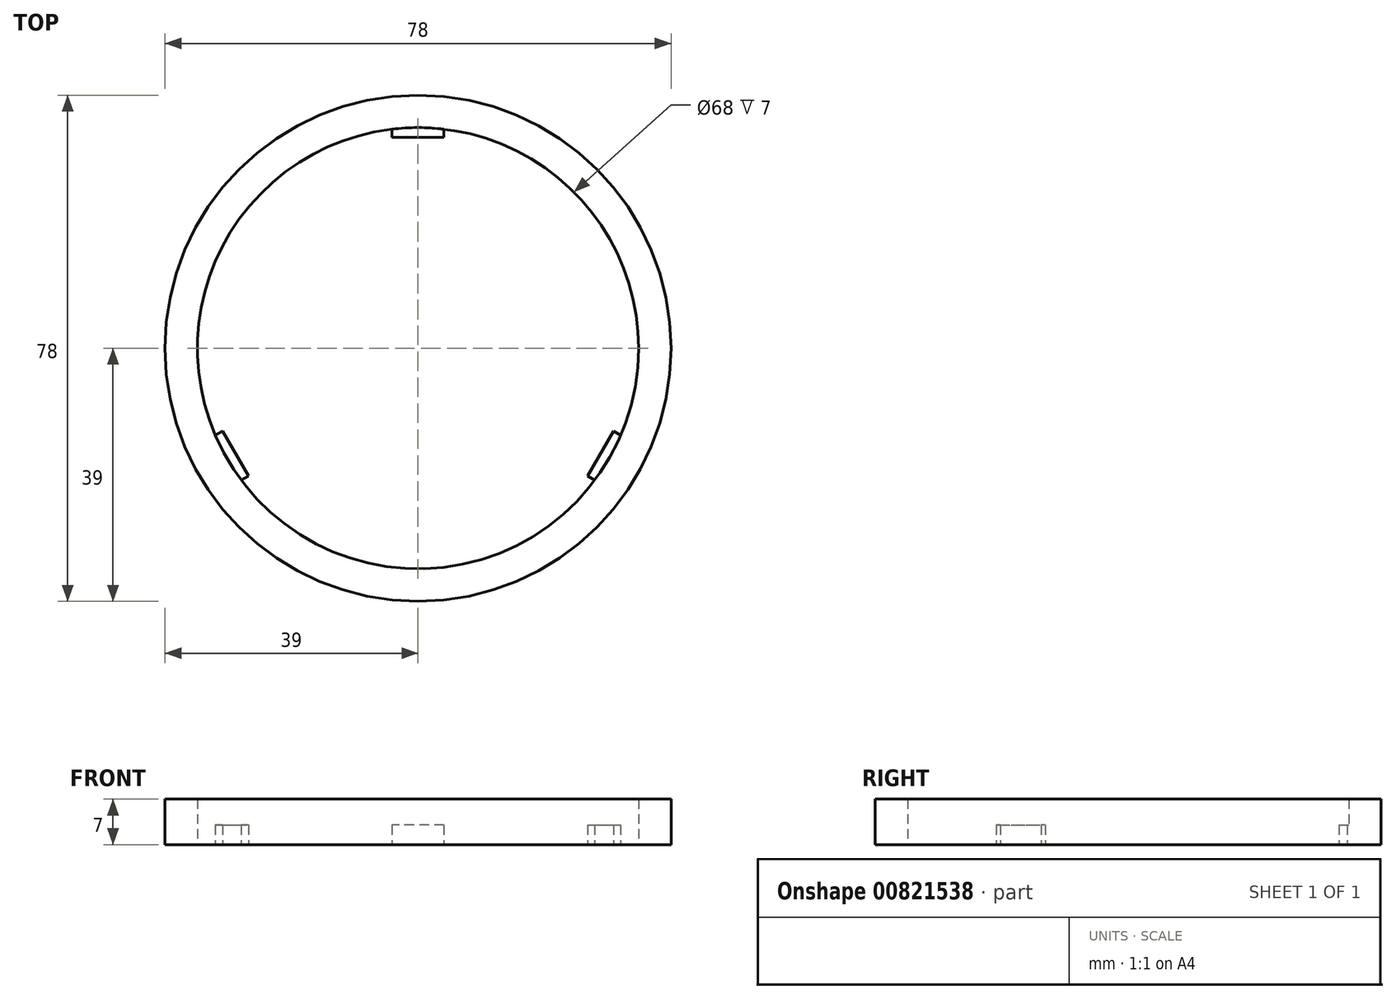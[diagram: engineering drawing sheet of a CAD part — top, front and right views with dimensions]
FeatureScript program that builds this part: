
annotation { "Feature Type Name" : "Feature", "Feature Type Description" : "" }
export const myFeature = defineFeature(function(context is Context, id is Id, definition is map)
    precondition{}
    {
        {
            var Q0;
            Q0=qCreatedBy(makeId("Top.planeOp"),FACE);
            var sketch = newSketch(context, id + "F0", { "sketchPlane" : qUnion([Q0])});
            skCircle(sketch, "E0", {"center": v(0, 0) * mm, "radius": 39 * mm});
            skCircle(sketch, "E1", {"center": v(0, 0) * mm, "radius": 34 * mm});
            skLineSegment(sketch, "E2.bottom", {"start": v(4, 32.5) * mm, "end": v(-4, 32.5) * mm});
            skLineSegment(sketch, "E2.left", {"start": v(4, 32.5) * mm, "end": v(4, 33.76) * mm});
            skLineSegment(sketch, "E2.right", {"start": v(-4, 32.5) * mm, "end": v(-4, 33.76) * mm});
            skPoint(sketch, "E2.middle", {"position": v(0, 34) * mm});
            skPoint(sketch, "E3.orphan", {"position": v(-4, 35.5) * mm});
            skPoint(sketch, "E4.orphan", {"position": v(4, 35.5) * mm});
            skLineSegment(sketch, "E5.1.0", {"start": v(-26.15, -19.71) * mm, "end": v(-27.24, -20.35) * mm});
            skLineSegment(sketch, "E5.1.1", {"start": v(-30.15, -12.79) * mm, "end": v(-26.15, -19.71) * mm});
            skLineSegment(sketch, "E5.1.2", {"start": v(-30.15, -12.79) * mm, "end": v(-31.24, -13.42) * mm});
            skLineSegment(sketch, "E5.2.0", {"start": v(30.15, -12.79) * mm, "end": v(31.24, -13.42) * mm});
            skLineSegment(sketch, "E5.2.1", {"start": v(26.15, -19.71) * mm, "end": v(30.15, -12.79) * mm});
            skLineSegment(sketch, "E5.2.2", {"start": v(26.15, -19.71) * mm, "end": v(27.24, -20.35) * mm});
            skSolve(sketch);
        }
        {
            var Q0;
            Q0 = qSketchRegion(id + "F0", true);
            extrude(context, id + "F1", {"entities" : qUnion([Q0]), "depth" : 7 * mm, "offsetDistance" : 25 * mm});
        }
        {
            var Q0;
            Q0=makeQuery(id+"F0.imprint","IMPRINT",FACE,{"disambiguationData":[TD([[makeQuery(id+"F0.imprint","IMPRINT",EDGE,{"derivedFrom":sQuery(id+"F0.wireOp",EDGE,"E2.bottom")}),-1.0]])]});
            extrude(context, id + "F2", {"entities" : qUnion([Q0]), "operationType" : NewBodyOperationType.ADD, "depth" : 3 * mm, "offsetDistance" : 25 * mm});
        }
        {
            var Q0;
            {var subQ0=sQuery(id+"F0.wireOp",EDGE,"E5.2.0");Q0=makeQuery(id+"F0.imprint","IMPRINT",FACE,{"disambiguationData":[TD([[makeQuery(id+"F0.imprint","IMPRINT",EDGE,{"derivedFrom":subQ0}),-1.0]])]});}
            extrude(context, id + "F3", {"entities" : qUnion([Q0]), "operationType" : NewBodyOperationType.ADD, "depth" : 3 * mm, "offsetDistance" : 25 * mm});
        }
        {
            var Q0;
            {var subQ0=sQuery(id+"F0.wireOp",EDGE,"E5.1.0");Q0=makeQuery(id+"F0.imprint","IMPRINT",FACE,{"disambiguationData":[TD([[makeQuery(id+"F0.imprint","IMPRINT",EDGE,{"derivedFrom":subQ0}),-1.0]])]});}
            extrude(context, id + "F4", {"entities" : qUnion([Q0]), "operationType" : NewBodyOperationType.ADD, "depth" : 3 * mm, "offsetDistance" : 25 * mm});
        }
    });
